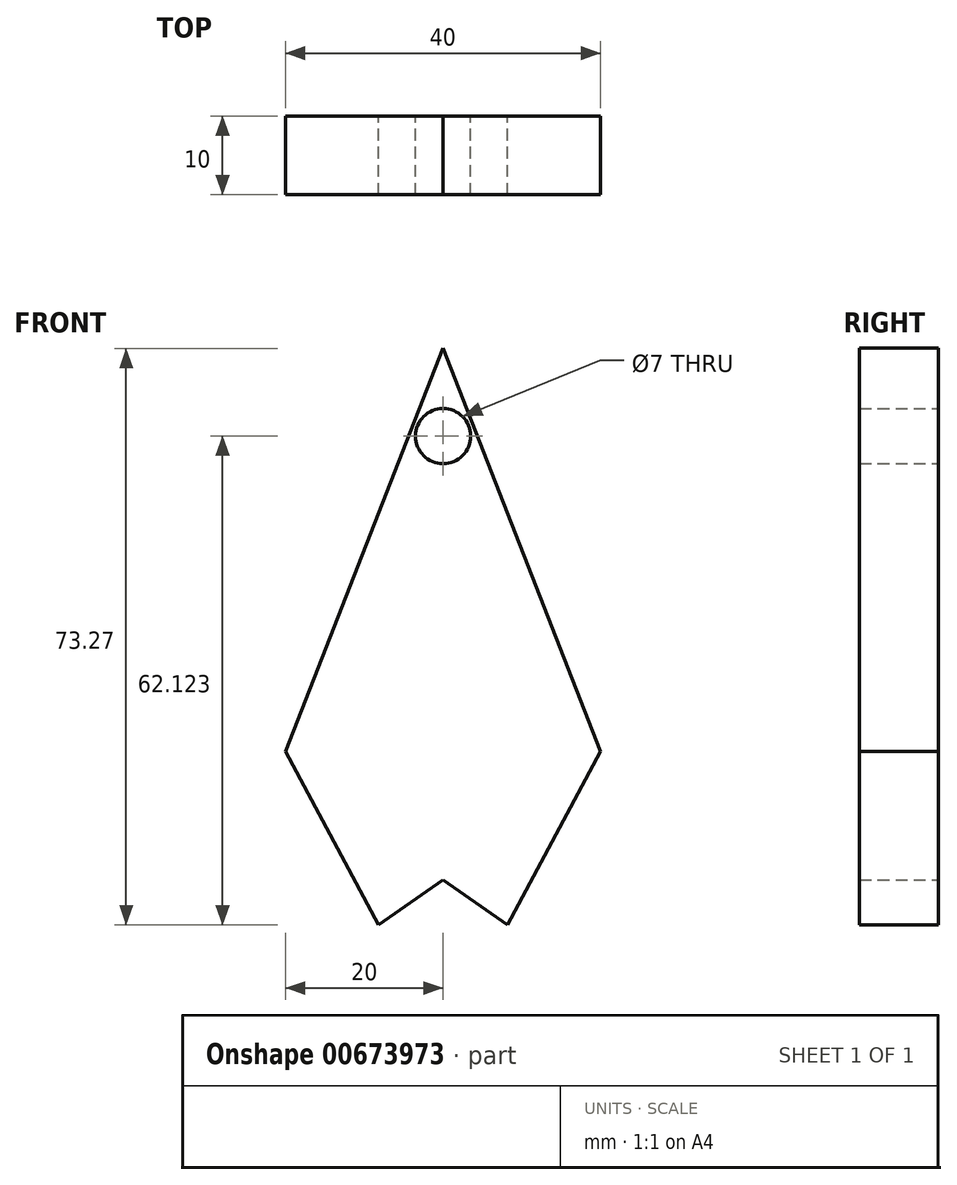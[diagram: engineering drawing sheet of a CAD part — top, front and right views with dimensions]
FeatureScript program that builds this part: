
annotation { "Feature Type Name" : "Feature", "Feature Type Description" : "" }
export const myFeature = defineFeature(function(context is Context, id is Id, definition is map)
    precondition{}
    {
        {
            var Q0;
            Q0=qCreatedBy(makeId("Front.planeOp"),FACE);
            var sketch = newSketch(context, id + "F0", { "sketchPlane" : qUnion([Q0])});
            skLineSegment(sketch, "E0", {"start": v(-20, 0) * mm, "end": v(0, 51.23) * mm});
            skLineSegment(sketch, "E1", {"start": v(0, 51.23) * mm, "end": v(20, 0) * mm});
            skLineSegment(sketch, "E2", {"start": v(8.2, -22.04) * mm, "end": v(20, 0) * mm});
            skLineSegment(sketch, "E3", {"start": v(-20, 0) * mm, "end": v(-8.2, -22.04) * mm});
            skLineSegment(sketch, "E4", {"start": v(-8.2, -22.04) * mm, "end": v(0, -16.32) * mm});
            skLineSegment(sketch, "E5", {"start": v(0, -16.32) * mm, "end": v(8.2, -22.04) * mm});
            skCircle(sketch, "E6", {"center": v(0, 40.08) * mm, "radius": 3.5 * mm});
            skSolve(sketch);
        }
        {
            var Q0;
            Q0 = qSketchRegion(id + "F0", true);
            extrude(context, id + "F1", {"entities" : qUnion([Q0]), "depth" : 10 * mm, "offsetDistance" : 25 * mm});
        }
    });
